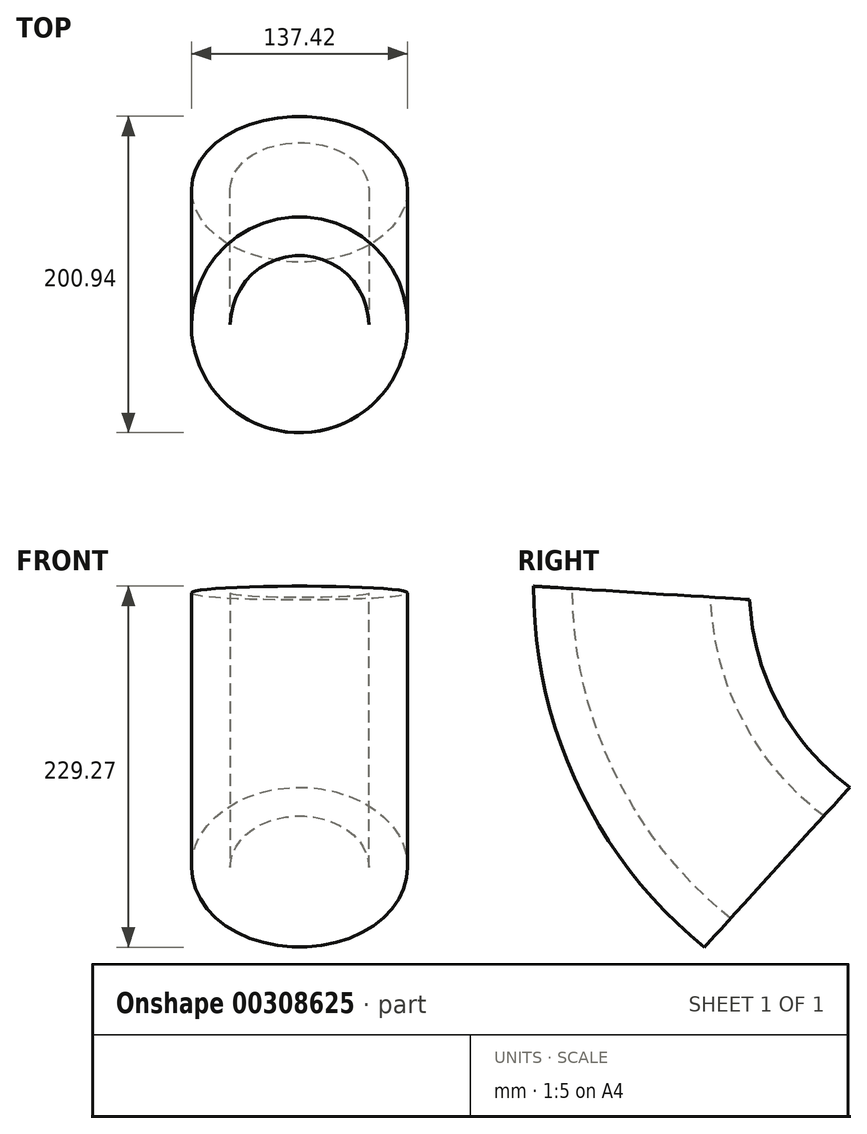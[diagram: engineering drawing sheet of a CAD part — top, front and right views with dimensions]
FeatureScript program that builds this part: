
annotation { "Feature Type Name" : "Feature", "Feature Type Description" : "" }
export const myFeature = defineFeature(function(context is Context, id is Id, definition is map)
    precondition{}
    {
        {
            var Q0;
            Q0=qCreatedBy(makeId("Right.planeOp"),FACE);
            var sketch = newSketch(context, id + "F0", { "sketchPlane" : qUnion([Q0])});
            skArc(sketch, "E0", {"start": v(-224.39, -16.6) * mm, "mid": v(-185.46, -127.4) * mm, "end": v(-95.99, -203.5) * mm});
            skArc(sketch, "E1", {"start": v(-155.62, -16.6) * mm, "mid": v(-137.68, -74.4) * mm, "end": v(-99.15, -121.08) * mm});
            skArc(sketch, "E2", {"start": v(-181, 0) * mm, "mid": v(-161.1, -82.5) * mm, "end": v(-105.8, -146.85) * mm});
            skArc(sketch, "E3", {"start": v(-293.5, 0) * mm, "mid": v(-268.54, -118.45) * mm, "end": v(-197.89, -216.75) * mm});
            skArc(sketch, "E4", {"start": v(-269, 0) * mm, "mid": v(-242.6, -116.22) * mm, "end": v(-168.58, -209.62) * mm});
            skLineSegment(sketch, "E5", {"start": v(-105.8, -146.85) * mm, "end": v(-168.58, -209.62) * mm, "construction": true});
            skLineSegment(sketch, "E6", {"start": v(-122.5, 0) * mm, "end": v(-140.7, 0) * mm});
            skLineSegment(sketch, "E7", {"start": v(-337.5, 10) * mm, "end": v(-337.5, 37) * mm});
            skLineSegment(sketch, "E8", {"start": v(-337.5, 37) * mm, "end": v(-112.5, 37) * mm});
            skLineSegment(sketch, "E9", {"start": v(-112.5, 37) * mm, "end": v(-112.5, 10) * mm});
            skLineSegment(sketch, "E10", {"start": v(-79.04, -120.08) * mm, "end": v(-60.13, -101.18) * mm});
            skLineSegment(sketch, "E11", {"start": v(-45.99, -101.18) * mm, "end": v(-26.9, -120.27) * mm});
            skLineSegment(sketch, "E12", {"start": v(-26.9, -120.27) * mm, "end": v(-63.98, -157.35) * mm});
            skLineSegment(sketch, "E13", {"start": v(-63.98, -157.35) * mm, "end": v(-56.9, -164.42) * mm});
            skLineSegment(sketch, "E14", {"start": v(-56.9, -164.42) * mm, "end": v(-148.83, -256.34) * mm});
            skLineSegment(sketch, "E15", {"start": v(-148.83, -256.34) * mm, "end": v(-155.9, -249.27) * mm});
            skLineSegment(sketch, "E16", {"start": v(-197.4, -238.44) * mm, "end": v(-205.09, -246.13) * mm});
            skLineSegment(sketch, "E17", {"start": v(-205.09, -260.27) * mm, "end": v(-186, -279.37) * mm});
            skLineSegment(sketch, "E18", {"start": v(-186, -279.37) * mm, "end": v(-155.9, -249.27) * mm});
            skPoint(sketch, "E19", {"position": v(-99.7, -207.2) * mm});
            skPoint(sketch, "E20.newPointA", {"position": v(-156.5, 0) * mm});
            skArc(sketch, "E20.filletArc", {"start": v(-140.7, 0) * mm, "mid": v(-151.86, -4.97) * mm, "end": v(-155.62, -16.6) * mm});
            skPoint(sketch, "E21.visualSharp", {"position": v(-88.22, -129.26) * mm});
            skArc(sketch, "E21.filletArc", {"start": v(-99.15, -121.08) * mm, "mid": v(-88.9, -124.46) * mm, "end": v(-79.04, -120.08) * mm});
            skPoint(sketch, "E22.visualSharp", {"position": v(-186, -227.04) * mm});
            skArc(sketch, "E22.filletArc", {"start": v(-197.4, -238.44) * mm, "mid": v(-193, -227.5) * mm, "end": v(-197.89, -216.75) * mm});
            skPoint(sketch, "E23.visualSharp", {"position": v(-212.16, -253.2) * mm});
            skPoint(sketch, "E24.visualSharp", {"position": v(-53.06, -94.1) * mm});
            skLineSegment(sketch, "E25", {"start": v(-327.5, 0) * mm, "end": v(-293.5, 0) * mm});
            skLineSegment(sketch, "E26", {"start": v(-269, 0) * mm, "end": v(-269, 37) * mm});
            skLineSegment(sketch, "E27", {"start": v(-181, 0) * mm, "end": v(-181, 37) * mm});
            skArc(sketch, "E28.filletArc", {"start": v(-205.09, -246.13) * mm, "mid": v(-208.02, -253.2) * mm, "end": v(-205.09, -260.27) * mm});
            skArc(sketch, "E29.filletArc", {"start": v(-45.99, -101.18) * mm, "mid": v(-53.06, -98.25) * mm, "end": v(-60.13, -101.18) * mm});
            skPoint(sketch, "E30.visualSharp", {"position": v(-112.5, 0) * mm});
            skArc(sketch, "E30.filletArc", {"start": v(-122.5, 0) * mm, "mid": v(-115.43, 2.93) * mm, "end": v(-112.5, 10) * mm});
            skPoint(sketch, "E31.visualSharp", {"position": v(-337.5, 0) * mm});
            skArc(sketch, "E31.filletArc", {"start": v(-337.5, 10) * mm, "mid": v(-334.57, 2.93) * mm, "end": v(-327.5, 0) * mm});
            skLineSegment(sketch, "E32", {"start": v(-137.25, -178.3) * mm, "end": v(-99.7, -207.2) * mm});
            skLineSegment(sketch, "E33", {"start": v(60.88, 0) * mm, "end": v(-418.43, 0) * mm, "construction": true});
            skLineSegment(sketch, "E34", {"start": v(-225, 0) * mm, "end": v(-225, 56) * mm, "construction": true});
            skLineSegment(sketch, "E35", {"start": v(-137.25, -178.3) * mm, "end": v(-94.02, -221.52) * mm, "construction": true});
            skLineSegment(sketch, "E36", {"start": v(-197.89, -216.75) * mm, "end": v(-99.15, -121.08) * mm});
            skLineSegment(sketch, "E37", {"start": v(-155.62, -16.6) * mm, "end": v(-293.03, -16.6) * mm});
            skLineSegment(sketch, "E38", {"start": v(-225, 37) * mm, "end": v(-225, -16.6) * mm});
            skLineSegment(sketch, "E39", {"start": v(-99.7, -207.2) * mm, "end": v(-153.52, -151.65) * mm});
            skPoint(sketch, "E40", {"position": v(-224.39, -16.6) * mm});
            skSolve(sketch);
        }
        {
            var Q0;
            Q0=sQuery(id+"F0.wireOp",EDGE,"E37");
            cPlane(context, id + "F1", {"entities" : qUnion([Q0]), "cplaneType" : CPlaneType.LINE_ANGLE, "offset" : 25 * mm, "angle" : 0 * degree, "width" : 150 * mm, "height" : 150 * mm});
        }
        {
            var Q0;
            Q0=qCreatedBy(id+"F1.planeOp",FACE);
            var sketch = newSketch(context, id + "F2", { "sketchPlane" : qUnion([Q0])});
            skPoint(sketch, "E41.0", {"position": v(0, 224.32) * mm});
            skPoint(sketch, "E42.0", {"position": v(0, 293.03) * mm});
            skPoint(sketch, "E43.0", {"position": v(0, 155.62) * mm});
            skCircle(sketch, "E44", {"center": v(0, 224.32) * mm, "radius": 68.7 * mm});
            skCircle(sketch, "E45", {"center": v(0, 224.32) * mm, "radius": 44 * mm});
            skSolve(sketch);
        }
        {
            var Q0;
            Q0=makeQuery(id+"F2.imprint","IMPRINT",FACE,{"disambiguationData":[TD([[makeQuery(id+"F2.imprint","IMPRINT",EDGE,{"derivedFrom":sQuery(id+"F2.wireOp",EDGE,"E44")}),1.0]])]});
            var Q1;
            Q1=sQuery(id+"F0.wireOp",EDGE,"E4");
            sweep(context, id + "F3", {"profiles" : qUnion([Q0]), "path" : qUnion([Q1])});
        }
    });
